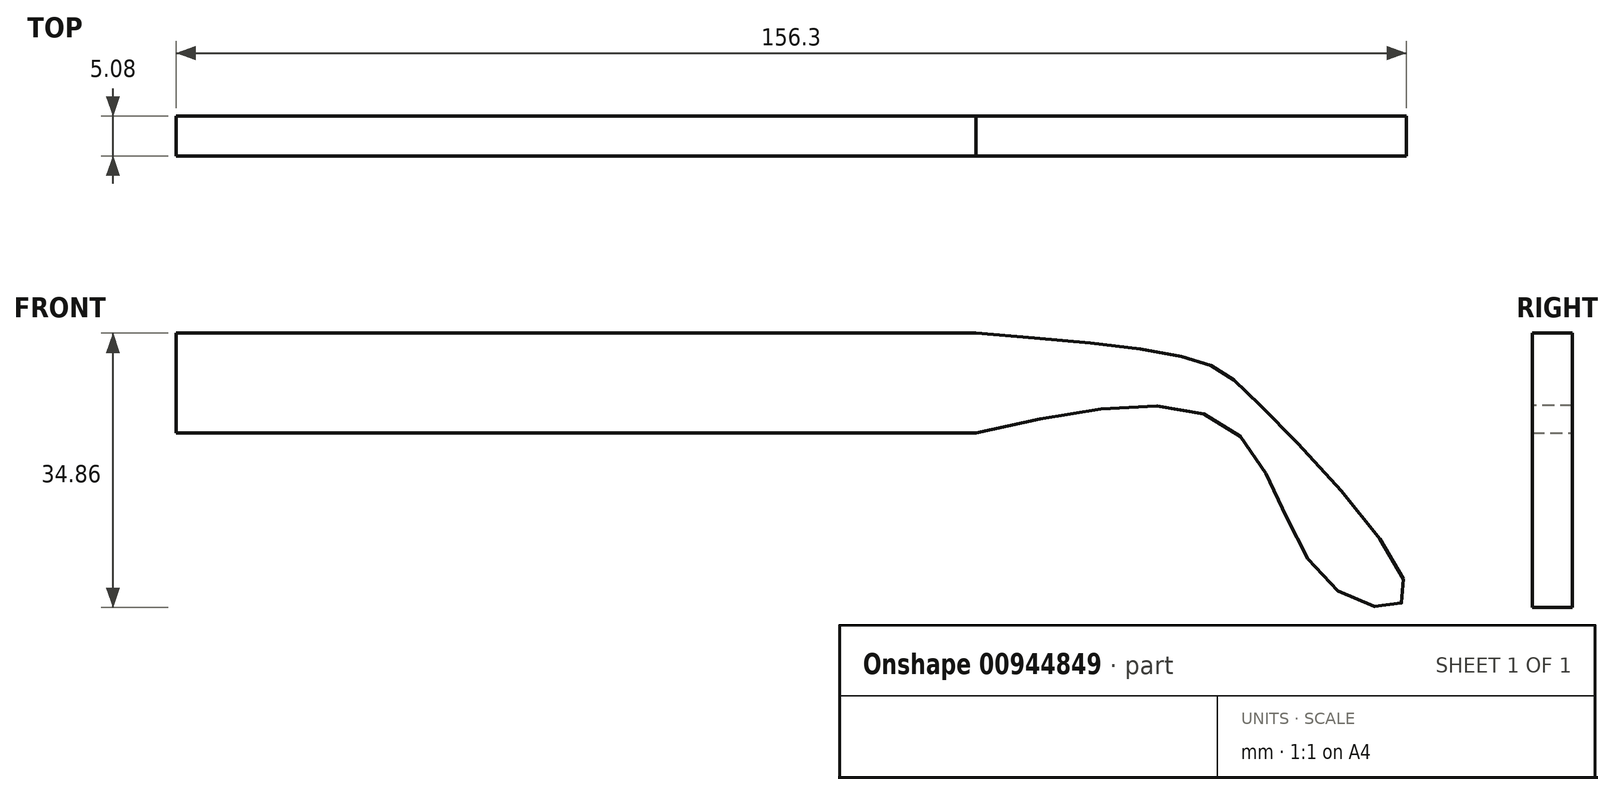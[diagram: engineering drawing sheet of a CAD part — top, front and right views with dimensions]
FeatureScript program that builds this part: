
annotation { "Feature Type Name" : "Feature", "Feature Type Description" : "" }
export const myFeature = defineFeature(function(context is Context, id is Id, definition is map)
    precondition{}
    {
        {
            var Q0;
            Q0=qCreatedBy(makeId("Front.planeOp"),FACE);
            var sketch = newSketch(context, id + "F0", { "sketchPlane" : qUnion([Q0])});
            skLineSegment(sketch, "E0.bottom", {"start": v(-50.8, 6.35) * mm, "end": v(50.8, 6.35) * mm});
            skLineSegment(sketch, "E0.top", {"start": v(-50.8, -6.35) * mm, "end": v(50.8, -6.35) * mm});
            skLineSegment(sketch, "E0.left", {"start": v(-50.8, 6.35) * mm, "end": v(-50.8, -6.35) * mm});
            skLineSegment(sketch, "E0.right", {"start": v(50.8, 6.35) * mm, "end": v(50.8, -6.35) * mm});
            skPoint(sketch, "E0.middle", {"position": v(0, 0) * mm});
            skFitSpline(sketch, "E1", {"points": [v(50.8, 6.35) * mm, v(78.59, 2.97) * mm, v(87.37, -3.2) * mm, v(105.41, -27.18) * mm, v(95.68, -25.52) * mm, v(83.33, -5.82) * mm, v(50.8, -6.35) * mm], "startDerivative": vector(173.7, -13.7) * mm, "endDerivative": vector(-188.38, -42.58) * mm});
            skSolve(sketch);
        }
        {
            var Q0;
            Q0=makeQuery(id+"F0.imprint","IMPRINT",FACE,{"disambiguationData":[TD([[makeQuery(id+"F0.imprint","IMPRINT",EDGE,{"derivedFrom":sQuery(id+"F0.wireOp",EDGE,"E0.bottom")}),-1.0]])]});
            var Q1;
            Q1=makeQuery(id+"F0.imprint","IMPRINT",FACE,{"disambiguationData":[TD([[makeQuery(id+"F0.imprint","IMPRINT",EDGE,{"derivedFrom":sQuery(id+"F0.wireOp",EDGE,"E0.right")}),1.0]])]});
            extrude(context, id + "F1", {"entities" : qUnion([Q0, Q1]), "depth" : 5.08 * mm, "offsetDistance" : 25.4 * mm});
        }
    });
